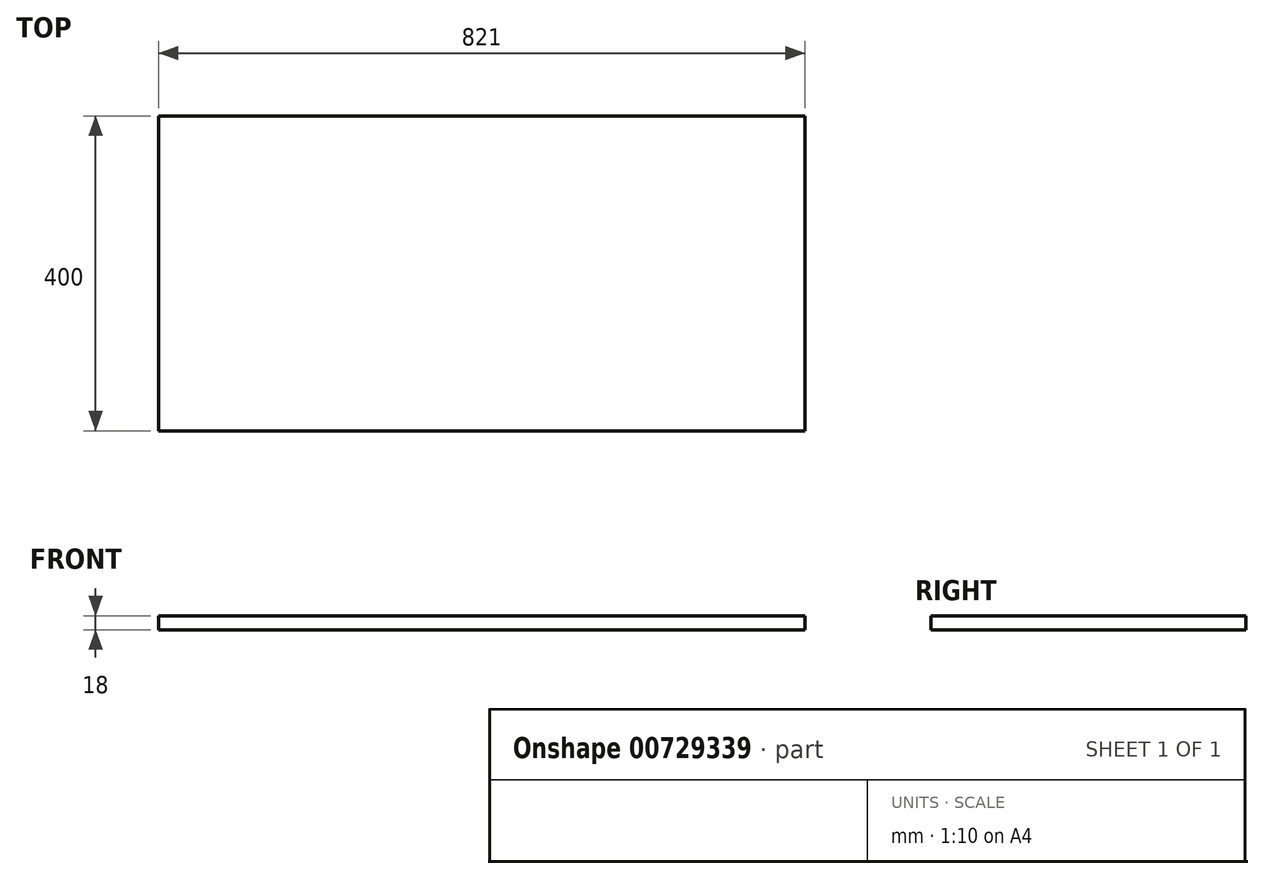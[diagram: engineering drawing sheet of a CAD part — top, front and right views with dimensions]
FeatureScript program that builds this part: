
annotation { "Feature Type Name" : "Feature", "Feature Type Description" : "" }
export const myFeature = defineFeature(function(context is Context, id is Id, definition is map)
    precondition{}
    {
        {
            var Q0;
            Q0=qCreatedBy(makeId("Front.planeOp"),FACE);
            var sketch = newSketch(context, id + "F0", { "sketchPlane" : qUnion([Q0])});
            skLineSegment(sketch, "E0.bottom", {"start": v(0, 0) * mm, "end": v(821, 0) * mm});
            skLineSegment(sketch, "E0.top", {"start": v(0, 18) * mm, "end": v(821, 18) * mm});
            skLineSegment(sketch, "E0.left", {"start": v(0, 0) * mm, "end": v(0, 18) * mm});
            skLineSegment(sketch, "E0.right", {"start": v(821, 0) * mm, "end": v(821, 18) * mm});
            skSolve(sketch);
        }
        {
            var Q0;
            Q0=makeQuery(id+"F0.imprint","IMPRINT",FACE,{"disambiguationData":[TD([[makeQuery(id+"F0.imprint","IMPRINT",EDGE,{"derivedFrom":sQuery(id+"F0.wireOp",EDGE,"E0.bottom")}),1.0]])]});
            extrude(context, id + "F1", {"entities" : qUnion([Q0]), "oppositeDirection" : true, "depth" : 400 * mm, "offsetDistance" : 25 * mm});
        }
    });
